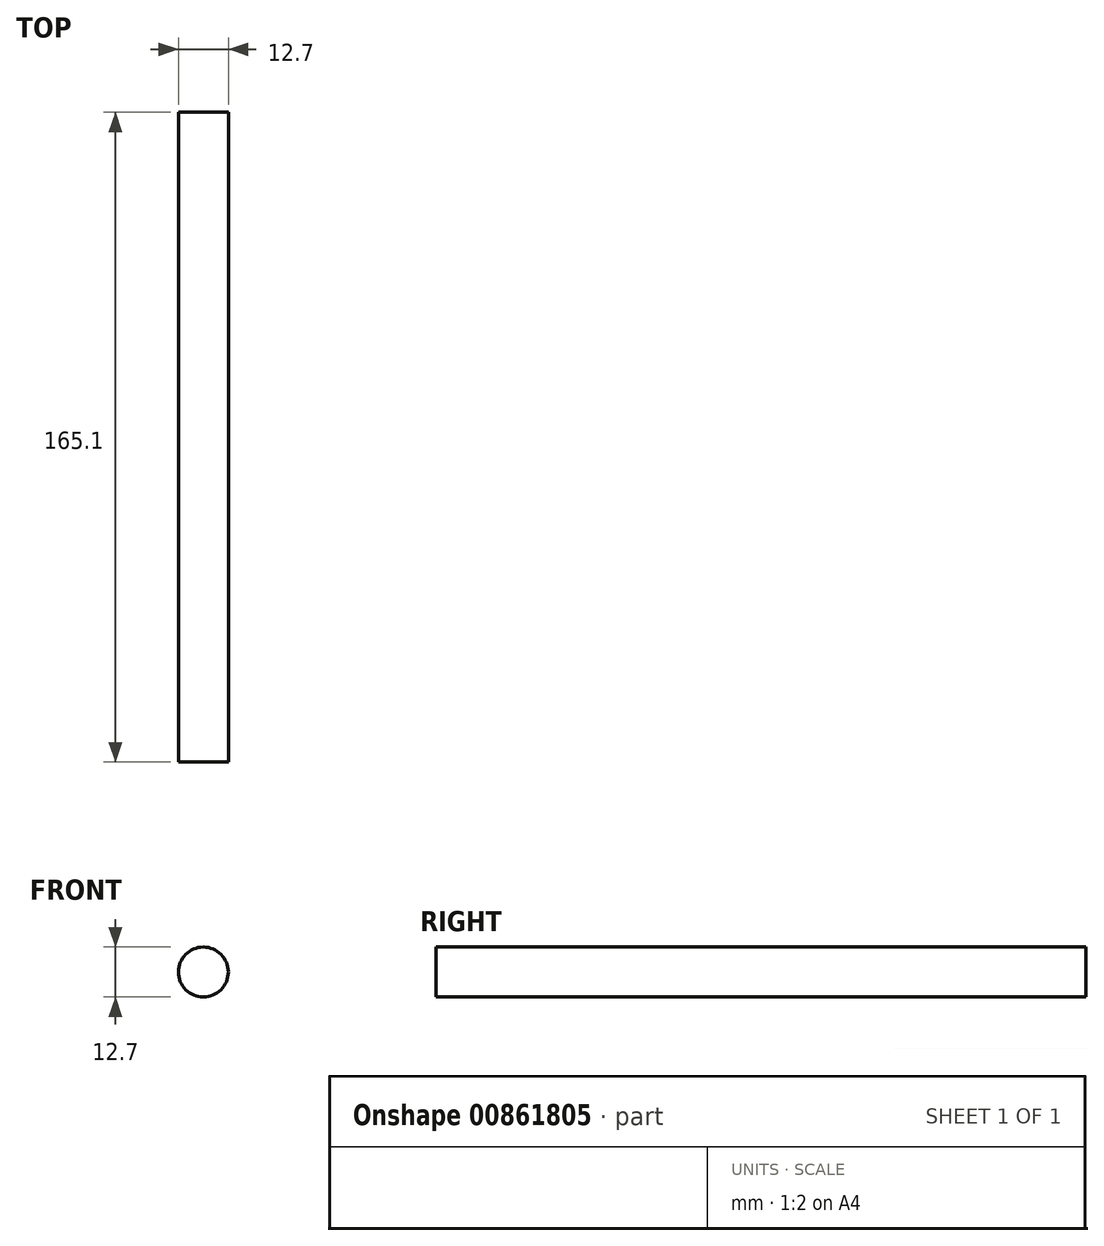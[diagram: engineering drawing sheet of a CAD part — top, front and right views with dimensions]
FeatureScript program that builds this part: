
annotation { "Feature Type Name" : "Feature", "Feature Type Description" : "" }
export const myFeature = defineFeature(function(context is Context, id is Id, definition is map)
    precondition{}
    {
        {
            var Q0;
            Q0=qCreatedBy(makeId("Front.planeOp"), FACE);
            var sketch = newSketch(context, id + "F0", { "sketchPlane" : qUnion([Q0])});
            skCircle(sketch, "E0", {"center": v(0, 0) * mm, "radius": 6.35 * mm});
            skSolve(sketch);
        }
        {
            var Q0;
            Q0 = qSketchRegion(id + "F0", true);
            extrude(context, id + "F1", {"entities" : qUnion([Q0]), "domain" : OperationDomain.MODEL, "flatOperationType" : FlatOperationType.REMOVE, "depth" : 165.1 * mm, "offsetDistance" : 25.4 * mm});
        }
    });
